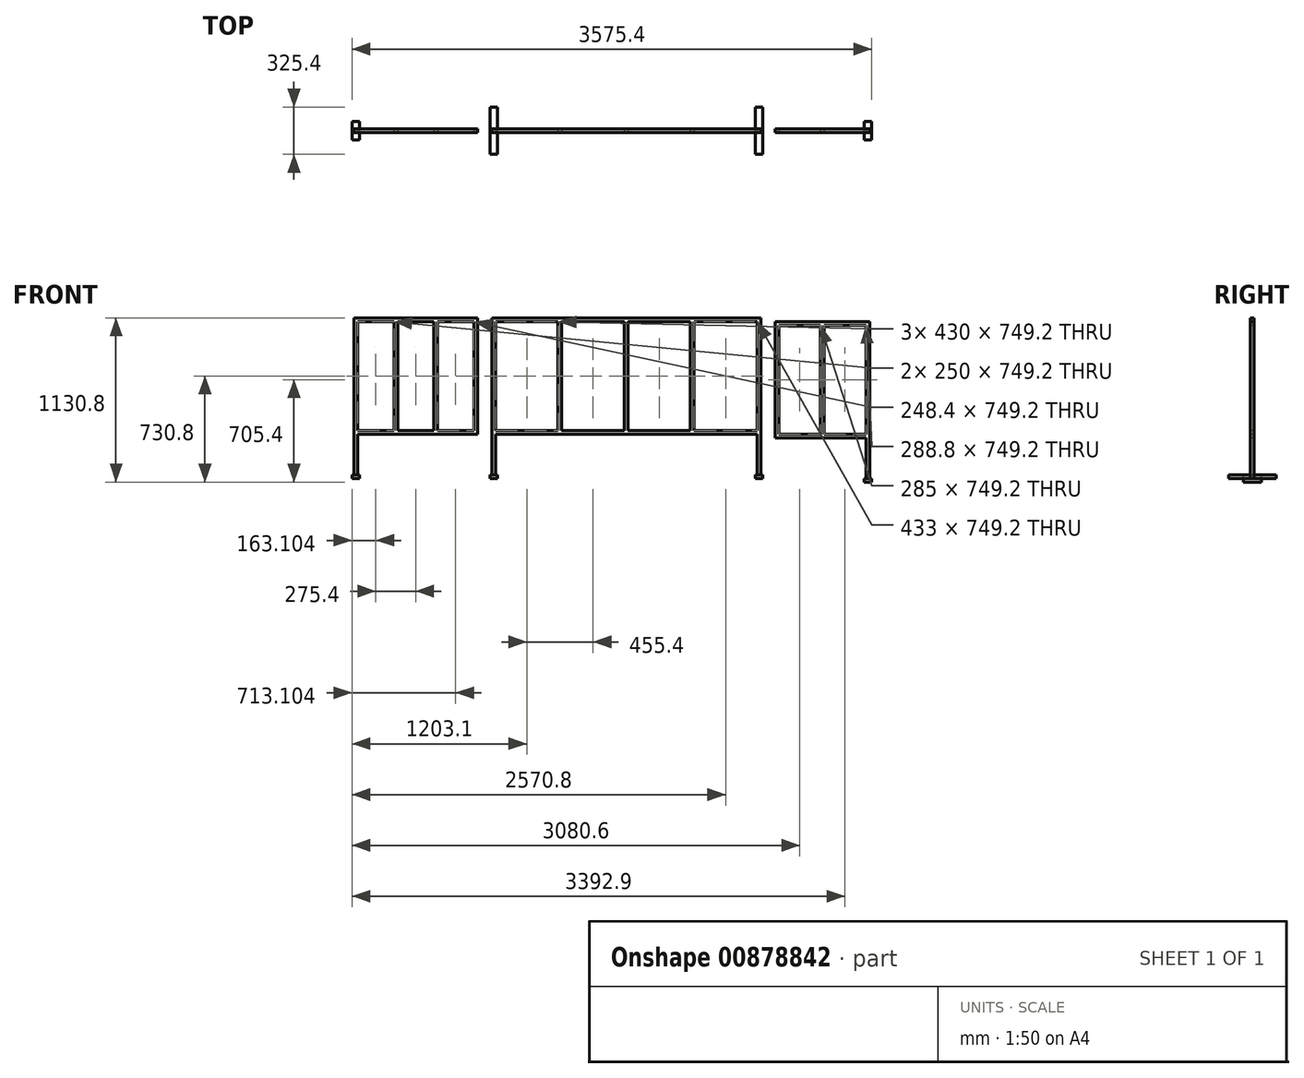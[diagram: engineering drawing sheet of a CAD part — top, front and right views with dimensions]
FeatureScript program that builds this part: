
annotation { "Feature Type Name" : "Feature", "Feature Type Description" : "" }
export const myFeature = defineFeature(function(context is Context, id is Id, definition is map)
    precondition{}
    {
        {
            var Q0;
            Q0=qCreatedBy(makeId("Front.planeOp"),FACE);
            var sketch = newSketch(context, id + "F0", { "sketchPlane" : qUnion([Q0])});
            skLineSegment(sketch, "E0.bottom", {"start": v(-686.66, -403.33) * mm, "end": v(1163.34, -403.33) * mm});
            skLineSegment(sketch, "E0.top", {"start": v(-686.66, 676.67) * mm, "end": v(1163.34, 676.67) * mm});
            skLineSegment(sketch, "E0.left", {"start": v(-686.66, -403.33) * mm, "end": v(-686.66, 676.67) * mm});
            skLineSegment(sketch, "E0.right", {"start": v(1163.34, -403.33) * mm, "end": v(1163.34, 676.67) * mm});
            skLineSegment(sketch, "E1.bottom", {"start": v(-661.26, -403.33) * mm, "end": v(1137.94, -403.33) * mm});
            skLineSegment(sketch, "E1.top", {"start": v(-661.26, -123.33) * mm, "end": v(1137.94, -123.33) * mm});
            skLineSegment(sketch, "E1.left", {"start": v(-661.26, -403.33) * mm, "end": v(-661.26, -123.33) * mm});
            skLineSegment(sketch, "E1.right", {"start": v(1137.94, -403.33) * mm, "end": v(1137.94, -123.33) * mm});
            skSolve(sketch);
        }
        {
            var Q0;
            Q0=makeQuery(id+"F0.imprint","IMPRINT",FACE,{"disambiguationData":[TD([[makeQuery(id+"F0.imprint","IMPRINT",EDGE,{"derivedFrom":sQuery(id+"F0.wireOp",EDGE,"E0.top")}),-1.0]])]});
            extrude(context, id + "F1", {"entities" : qUnion([Q0]), "oppositeDirection" : true, "depth" : 25.4 * mm, "offsetDistance" : 25 * mm});
        }
        {
            var Q0;
            Q0=makeQuery(id+"F1.opExtrude","CAP_FACE",FACE,{"disambiguationData":[OSD([sQuery(id+"F0.wireOp",EDGE,"E0.bottom"),sQuery(id+"F0.wireOp",EDGE,"E0.top"),sQuery(id+"F0.wireOp",EDGE,"E0.left"),sQuery(id+"F0.wireOp",EDGE,"E0.right"),sQuery(id+"F0.wireOp",EDGE,"E1.top"),sQuery(id+"F0.wireOp",EDGE,"E1.left"),sQuery(id+"F0.wireOp",EDGE,"E1.right")])],"isStart":true});
            var sketch = newSketch(context, id + "F2", { "sketchPlane" : qUnion([Q0])});
            skLineSegment(sketch, "E2.bottom", {"start": v(-661.26, 651.27) * mm, "end": v(-231.26, 651.27) * mm});
            skLineSegment(sketch, "E2.top", {"start": v(-661.26, -97.93) * mm, "end": v(-231.26, -97.93) * mm});
            skLineSegment(sketch, "E2.left", {"start": v(-661.26, 651.27) * mm, "end": v(-661.26, -97.93) * mm});
            skLineSegment(sketch, "E2.right", {"start": v(-231.26, 651.27) * mm, "end": v(-231.26, -97.93) * mm});
            skLineSegment(sketch, "E3.bottom", {"start": v(-205.86, 651.27) * mm, "end": v(224.14, 651.27) * mm});
            skLineSegment(sketch, "E3.top", {"start": v(-205.86, -97.93) * mm, "end": v(224.14, -97.93) * mm});
            skLineSegment(sketch, "E3.left", {"start": v(-205.86, 651.27) * mm, "end": v(-205.86, -97.93) * mm});
            skLineSegment(sketch, "E3.right", {"start": v(224.14, 651.27) * mm, "end": v(224.14, -97.93) * mm});
            skLineSegment(sketch, "E4.bottom", {"start": v(249.54, 651.27) * mm, "end": v(679.54, 651.27) * mm});
            skLineSegment(sketch, "E4.top", {"start": v(249.54, -97.93) * mm, "end": v(679.54, -97.93) * mm});
            skLineSegment(sketch, "E4.left", {"start": v(249.54, 651.27) * mm, "end": v(249.54, -97.93) * mm});
            skLineSegment(sketch, "E4.right", {"start": v(679.54, 651.27) * mm, "end": v(679.54, -97.93) * mm});
            skLineSegment(sketch, "E5.bottom", {"start": v(704.94, 651.27) * mm, "end": v(1137.94, 651.27) * mm});
            skLineSegment(sketch, "E5.top", {"start": v(704.94, -97.93) * mm, "end": v(1137.94, -97.93) * mm});
            skLineSegment(sketch, "E5.left", {"start": v(704.94, 651.27) * mm, "end": v(704.94, -97.93) * mm});
            skLineSegment(sketch, "E5.right", {"start": v(1137.94, 651.27) * mm, "end": v(1137.94, -97.93) * mm});
            skSolve(sketch);
        }
        {
            var Q0;
            Q0=makeQuery(id+"F2.imprint","IMPRINT",FACE,{"disambiguationData":[TD([[makeQuery(id+"F2.imprint","IMPRINT",EDGE,{"derivedFrom":sQuery(id+"F2.wireOp",EDGE,"E3.bottom")}),-1.0]])]});
            var Q1;
            Q1=makeQuery(id+"F2.imprint","IMPRINT",FACE,{"disambiguationData":[TD([[makeQuery(id+"F2.imprint","IMPRINT",EDGE,{"derivedFrom":sQuery(id+"F2.wireOp",EDGE,"E4.bottom")}),-1.0]])]});
            var Q2;
            Q2=makeQuery(id+"F2.imprint","IMPRINT",FACE,{"disambiguationData":[TD([[makeQuery(id+"F2.imprint","IMPRINT",EDGE,{"derivedFrom":sQuery(id+"F2.wireOp",EDGE,"E5.bottom")}),-1.0]])]});
            var Q3;
            Q3=makeQuery(id+"F2.imprint","IMPRINT",FACE,{"disambiguationData":[TD([[makeQuery(id+"F2.imprint","IMPRINT",EDGE,{"derivedFrom":sQuery(id+"F2.wireOp",EDGE,"E2.bottom")}),-1.0]])]});
            extrude(context, id + "F3", {"entities" : qUnion([Q0, Q1, Q2, Q3]), "operationType" : NewBodyOperationType.REMOVE, "oppositeDirection" : true, "depth" : 25.4 * mm, "offsetDistance" : 25 * mm});
        }
        {
            var Q0;
            {var subQ0=sQuery(id+"F0.wireOp",EDGE,"E0.bottom");Q0=makeQuery(id+"F1.opExtrude","SWEPT_FACE",FACE,{"disambiguationData":[OSD([subQ0]),TDD([makeQuery(id+"F0.imprint","IMPRINT",EDGE,{"disambiguationData":[TD([[makeQuery(id+"F0.imprint","INTERSECT",VERTEX,{"derivedFrom":[subQ0,sQuery(id+"F0.wireOp",EDGE,"E0.right")]}),1.0]])],"derivedFrom":subQ0})])]});}
            var sketch = newSketch(context, id + "F4", { "sketchPlane" : qUnion([Q0])});
            skLineSegment(sketch, "E6.bottom", {"start": v(1125.24, 150) * mm, "end": v(1176.04, 150) * mm});
            skLineSegment(sketch, "E6.top", {"start": v(1125.24, -175.4) * mm, "end": v(1176.04, -175.4) * mm});
            skLineSegment(sketch, "E6.left", {"start": v(1125.24, 150) * mm, "end": v(1125.24, -175.4) * mm});
            skLineSegment(sketch, "E6.right", {"start": v(1176.04, 150) * mm, "end": v(1176.04, -175.4) * mm});
            skLineSegment(sketch, "E7.1.0.0", {"start": v(-699.36, 150) * mm, "end": v(-699.36, -175.4) * mm});
            skLineSegment(sketch, "E7.1.0.1", {"start": v(-648.56, 150) * mm, "end": v(-648.56, -175.4) * mm});
            skLineSegment(sketch, "E7.1.0.2", {"start": v(-699.36, -175.4) * mm, "end": v(-648.56, -175.4) * mm});
            skLineSegment(sketch, "E7.1.0.3", {"start": v(-699.36, 150) * mm, "end": v(-648.56, 150) * mm});
            skLineSegment(sketch, "E7.direction1", {"start": v(1125.24, -175.4) * mm, "end": v(-699.36, -175.4) * mm, "construction": true});
            skSolve(sketch);
        }
        {
            var Q0;
            Q0 = qSketchRegion(id + "F4", true);
            extrude(context, id + "F5", {"entities" : qUnion([Q0]), "operationType" : NewBodyOperationType.ADD, "depth" : 25.4 * mm, "offsetDistance" : 25 * mm});
        }
        {
            var Q0;
            Q0=makeQuery(id+"F1.opExtrude","CAP_FACE",FACE,{"disambiguationData":[OSD([sQuery(id+"F0.wireOp",EDGE,"E0.bottom"),sQuery(id+"F0.wireOp",EDGE,"E0.top"),sQuery(id+"F0.wireOp",EDGE,"E0.left"),sQuery(id+"F0.wireOp",EDGE,"E0.right"),sQuery(id+"F0.wireOp",EDGE,"E1.top"),sQuery(id+"F0.wireOp",EDGE,"E1.left"),sQuery(id+"F0.wireOp",EDGE,"E1.right")])],"isStart":true});
            var sketch = newSketch(context, id + "F6", { "sketchPlane" : qUnion([Q0])});
            skLineSegment(sketch, "E8.bottom", {"start": v(1263.34, 651.27) * mm, "end": v(1913.34, 651.27) * mm});
            skLineSegment(sketch, "E8.top", {"start": v(1263.34, -428.73) * mm, "end": v(1913.34, -428.73) * mm});
            skLineSegment(sketch, "E8.left", {"start": v(1263.34, 651.27) * mm, "end": v(1263.34, -428.73) * mm});
            skLineSegment(sketch, "E8.right", {"start": v(1913.34, 651.27) * mm, "end": v(1913.34, -428.73) * mm});
            skLineSegment(sketch, "E9.bottom", {"start": v(1263.34, -428.73) * mm, "end": v(1887.94, -428.73) * mm});
            skLineSegment(sketch, "E9.top", {"start": v(1263.34, -148.73) * mm, "end": v(1887.94, -148.73) * mm});
            skLineSegment(sketch, "E9.left", {"start": v(1263.34, -428.73) * mm, "end": v(1263.34, -148.73) * mm});
            skLineSegment(sketch, "E9.right", {"start": v(1887.94, -428.73) * mm, "end": v(1887.94, -148.73) * mm});
            skSolve(sketch);
        }
        {
            var Q0;
            Q0=makeQuery(id+"F6.imprint","IMPRINT",FACE,{"disambiguationData":[TD([[makeQuery(id+"F6.imprint","IMPRINT",EDGE,{"derivedFrom":sQuery(id+"F6.wireOp",EDGE,"E8.bottom")}),-1.0]])]});
            extrude(context, id + "F7", {"entities" : qUnion([Q0]), "oppositeDirection" : true, "depth" : 25 * mm, "offsetDistance" : 25 * mm});
        }
        {
            var Q0;
            Q0=makeQuery(id+"F7.opExtrude","CAP_FACE",FACE,{"disambiguationData":[OSD([sQuery(id+"F6.wireOp",EDGE,"E8.bottom"),sQuery(id+"F6.wireOp",EDGE,"E8.top"),sQuery(id+"F6.wireOp",EDGE,"E8.left"),sQuery(id+"F6.wireOp",EDGE,"E8.right"),sQuery(id+"F6.wireOp",EDGE,"E9.top"),sQuery(id+"F6.wireOp",EDGE,"E9.left"),sQuery(id+"F6.wireOp",EDGE,"E9.right")])],"isStart":true});
            var sketch = newSketch(context, id + "F8", { "sketchPlane" : qUnion([Q0])});
            skLineSegment(sketch, "E10.bottom", {"start": v(1288.74, 625.87) * mm, "end": v(1573.74, 625.87) * mm});
            skLineSegment(sketch, "E10.top", {"start": v(1288.74, -123.33) * mm, "end": v(1573.74, -123.33) * mm});
            skLineSegment(sketch, "E10.left", {"start": v(1288.74, 625.87) * mm, "end": v(1288.74, -123.33) * mm});
            skLineSegment(sketch, "E10.right", {"start": v(1573.74, 625.87) * mm, "end": v(1573.74, -123.33) * mm});
            skLineSegment(sketch, "E11.bottom", {"start": v(1599.14, 625.87) * mm, "end": v(1887.94, 625.87) * mm});
            skLineSegment(sketch, "E11.top", {"start": v(1599.14, -123.33) * mm, "end": v(1887.94, -123.33) * mm});
            skLineSegment(sketch, "E11.left", {"start": v(1599.14, 625.87) * mm, "end": v(1599.14, -123.33) * mm});
            skLineSegment(sketch, "E11.right", {"start": v(1887.94, 625.87) * mm, "end": v(1887.94, -123.33) * mm});
            skSolve(sketch);
        }
        {
            var Q0;
            Q0 = qSketchRegion(id + "F8", true);
            extrude(context, id + "F9", {"entities" : qUnion([Q0]), "operationType" : NewBodyOperationType.REMOVE, "oppositeDirection" : true, "depth" : 26 * mm, "offsetDistance" : 25 * mm});
        }
        {
            var Q0;
            Q0=makeQuery(id+"F1.opExtrude","CAP_FACE",FACE,{"disambiguationData":[OSD([sQuery(id+"F0.wireOp",EDGE,"E0.bottom"),sQuery(id+"F0.wireOp",EDGE,"E0.top"),sQuery(id+"F0.wireOp",EDGE,"E0.left"),sQuery(id+"F0.wireOp",EDGE,"E0.right"),sQuery(id+"F0.wireOp",EDGE,"E1.top"),sQuery(id+"F0.wireOp",EDGE,"E1.left"),sQuery(id+"F0.wireOp",EDGE,"E1.right")])],"isStart":true});
            var sketch = newSketch(context, id + "F10", { "sketchPlane" : qUnion([Q0])});
            skLineSegment(sketch, "E12.bottom", {"start": v(-786.66, 676.67) * mm, "end": v(-1636.66, 676.67) * mm});
            skLineSegment(sketch, "E12.top", {"start": v(-786.66, -403.33) * mm, "end": v(-1636.66, -403.33) * mm});
            skLineSegment(sketch, "E12.left", {"start": v(-786.66, 676.67) * mm, "end": v(-786.66, -403.33) * mm});
            skLineSegment(sketch, "E12.right", {"start": v(-1636.66, 676.67) * mm, "end": v(-1636.66, -403.33) * mm});
            skLineSegment(sketch, "E13.bottom", {"start": v(-1611.26, -123.33) * mm, "end": v(-786.66, -123.33) * mm});
            skLineSegment(sketch, "E13.top", {"start": v(-1611.26, -403.33) * mm, "end": v(-786.66, -403.33) * mm});
            skLineSegment(sketch, "E13.left", {"start": v(-1611.26, -123.33) * mm, "end": v(-1611.26, -403.33) * mm});
            skLineSegment(sketch, "E13.right", {"start": v(-786.66, -123.33) * mm, "end": v(-786.66, -403.33) * mm});
            skLineSegment(sketch, "E14.bottom", {"start": v(-1611.26, 651.27) * mm, "end": v(-1361.26, 651.27) * mm});
            skLineSegment(sketch, "E14.top", {"start": v(-1611.26, -97.93) * mm, "end": v(-1361.26, -97.93) * mm});
            skLineSegment(sketch, "E14.left", {"start": v(-1611.26, 651.27) * mm, "end": v(-1611.26, -97.93) * mm});
            skLineSegment(sketch, "E14.right", {"start": v(-1361.26, 651.27) * mm, "end": v(-1361.26, -97.93) * mm});
            skLineSegment(sketch, "E15.bottom", {"start": v(-1335.86, 651.27) * mm, "end": v(-1085.86, 651.27) * mm});
            skLineSegment(sketch, "E15.top", {"start": v(-1335.86, -97.93) * mm, "end": v(-1085.86, -97.93) * mm});
            skLineSegment(sketch, "E15.left", {"start": v(-1335.86, 651.27) * mm, "end": v(-1335.86, -97.93) * mm});
            skLineSegment(sketch, "E15.right", {"start": v(-1085.86, 651.27) * mm, "end": v(-1085.86, -97.93) * mm});
            skLineSegment(sketch, "E16.bottom", {"start": v(-1060.46, 651.27) * mm, "end": v(-812.06, 651.27) * mm});
            skLineSegment(sketch, "E16.top", {"start": v(-1060.46, -97.93) * mm, "end": v(-812.06, -97.93) * mm});
            skLineSegment(sketch, "E16.left", {"start": v(-1060.46, 651.27) * mm, "end": v(-1060.46, -97.93) * mm});
            skLineSegment(sketch, "E16.right", {"start": v(-812.06, 651.27) * mm, "end": v(-812.06, -97.93) * mm});
            skSolve(sketch);
        }
        {
            var Q0;
            Q0=makeQuery(id+"F10.imprint","IMPRINT",FACE,{"disambiguationData":[TD([[makeQuery(id+"F10.imprint","IMPRINT",EDGE,{"derivedFrom":sQuery(id+"F10.wireOp",EDGE,"E12.bottom")}),1.0]])]});
            extrude(context, id + "F11", {"entities" : qUnion([Q0]), "oppositeDirection" : true, "depth" : 25.4 * mm, "offsetDistance" : 25 * mm});
        }
        {
            var Q0;
            Q0=makeQuery(id+"F7.opExtrude","SWEPT_FACE",FACE,{"disambiguationData":[OSD([sQuery(id+"F6.wireOp",EDGE,"E8.top")])]});
            var sketch = newSketch(context, id + "F12", { "sketchPlane" : qUnion([Q0])});
            skLineSegment(sketch, "E17.bottom", {"start": v(1875.24, 50) * mm, "end": v(1926.04, 50) * mm});
            skLineSegment(sketch, "E17.top", {"start": v(1875.24, -75) * mm, "end": v(1926.04, -75) * mm});
            skLineSegment(sketch, "E17.left", {"start": v(1875.24, 50) * mm, "end": v(1875.24, -75) * mm});
            skLineSegment(sketch, "E17.right", {"start": v(1926.04, 50) * mm, "end": v(1926.04, -75) * mm});
            skSolve(sketch);
        }
        {
            var Q0;
            Q0 = qSketchRegion(id + "F12", true);
            extrude(context, id + "F13", {"entities" : qUnion([Q0]), "operationType" : NewBodyOperationType.ADD, "depth" : 25.4 * mm, "offsetDistance" : 25 * mm});
        }
        {
            var Q0;
            Q0=makeQuery(id+"F11.opExtrude","SWEPT_FACE",FACE,{"disambiguationData":[OSD([sQuery(id+"F10.wireOp",EDGE,"E12.top")])]});
            var sketch = newSketch(context, id + "F14", { "sketchPlane" : qUnion([Q0])});
            skLineSegment(sketch, "E18.bottom", {"start": v(-1649.36, 50) * mm, "end": v(-1598.56, 50) * mm});
            skLineSegment(sketch, "E18.top", {"start": v(-1649.36, -75.4) * mm, "end": v(-1598.56, -75.4) * mm});
            skLineSegment(sketch, "E18.left", {"start": v(-1649.36, 50) * mm, "end": v(-1649.36, -75.4) * mm});
            skLineSegment(sketch, "E18.right", {"start": v(-1598.56, 50) * mm, "end": v(-1598.56, -75.4) * mm});
            skSolve(sketch);
        }
        {
            var Q0;
            Q0 = qSketchRegion(id + "F14", true);
            extrude(context, id + "F15", {"entities" : qUnion([Q0]), "operationType" : NewBodyOperationType.ADD, "depth" : 25.4 * mm, "offsetDistance" : 25 * mm});
        }
    });
